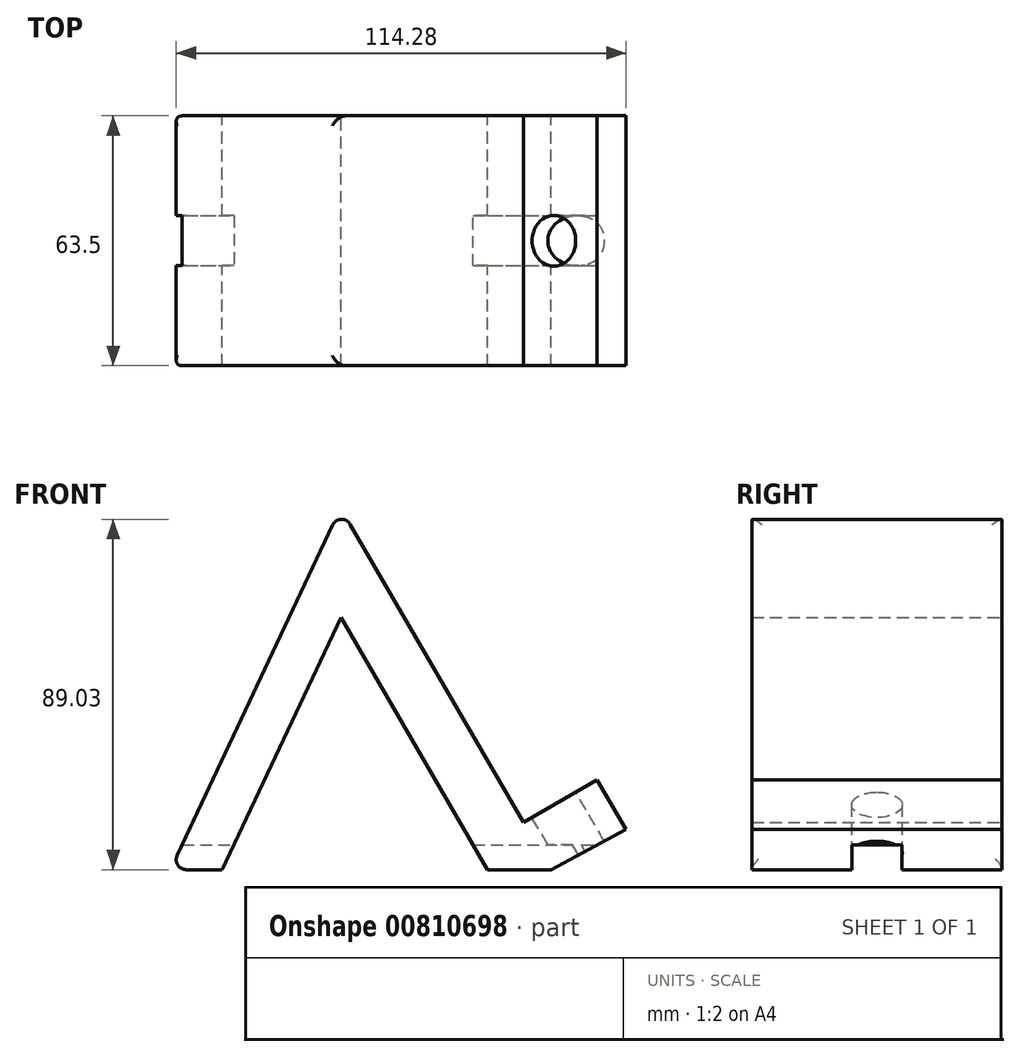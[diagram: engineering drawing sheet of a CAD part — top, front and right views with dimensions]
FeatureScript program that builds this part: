
annotation { "Feature Type Name" : "Feature", "Feature Type Description" : "" }
export const myFeature = defineFeature(function(context is Context, id is Id, definition is map)
    precondition{}
    {
        {
            var Q0;
            Q0=qCreatedBy(makeId("Front.planeOp"),FACE);
            var sketch = newSketch(context, id + "F0", { "sketchPlane" : qUnion([Q0])});
            skPoint(sketch, "E0.end.orphan", {"position": v(14.83, 0) * mm});
            skPoint(sketch, "E0.start.orphan", {"position": v(21.6, 0) * mm});
            skPoint(sketch, "E1.end.orphan", {"position": v(-8.7, 0) * mm});
            skPoint(sketch, "E2.end.orphan", {"position": v(-15.4, 9.9) * mm});
            skPoint(sketch, "E3.end.orphan", {"position": v(-27.26, 0) * mm});
            skPoint(sketch, "E4.end.orphan", {"position": v(-22.1, 19.8) * mm});
            skLineSegment(sketch, "E5", {"start": v(39.33, -93.18) * mm, "end": v(-7.17, -13.23) * mm});
            skLineSegment(sketch, "E6", {"start": v(-7.17, -13.23) * mm, "end": v(-50.38, -105.18) * mm});
            skPoint(sketch, "E7.end.orphan", {"position": v(-10.8, -21.16) * mm});
            skPoint(sketch, "E8.orphan", {"position": v(38.06, -105.18) * mm});
            skLineSegment(sketch, "E9", {"start": v(-10.8, -20.96) * mm, "end": v(-10.8, -21.16) * mm});
            skLineSegment(sketch, "E10", {"start": v(-50.38, -105.18) * mm, "end": v(-37.22, -105.18) * mm});
            skLineSegment(sketch, "E11", {"start": v(-37.22, -105.18) * mm, "end": v(-7.1, -41.1) * mm});
            skLineSegment(sketch, "E12", {"start": v(-7.1, -41.1) * mm, "end": v(30.16, -105.18) * mm});
            skLineSegment(sketch, "E13", {"start": v(30.16, -105.18) * mm, "end": v(46.3, -105.18) * mm});
            skPoint(sketch, "E14.end.orphan", {"position": v(-10.8, 22.67) * mm});
            skLineSegment(sketch, "E15", {"start": v(39.33, -93.18) * mm, "end": v(58, -82.32) * mm});
            skLineSegment(sketch, "E16", {"start": v(58, -82.32) * mm, "end": v(65.36, -94.95) * mm});
            skLineSegment(sketch, "E17", {"start": v(65.36, -94.95) * mm, "end": v(46.3, -105.18) * mm});
            skPoint(sketch, "E18.start.orphan", {"position": v(-71.03, -105.18) * mm});
            skLineSegment(sketch, "E19", {"start": v(-7.17, -13.23) * mm, "end": v(39.33, -93.18) * mm});
            skSolve(sketch);
        }
        {
            var Q0;
            Q0 = qSketchRegion(id + "F0", true);
            extrude(context, id + "F1", {"entities" : qUnion([Q0]), "depth" : 63.5 * mm, "offsetDistance" : 25.4 * mm});
        }
        {
            var Q0;
            Q0=makeQuery(id+"F1.opExtrude","SWEPT_FACE",FACE,{"disambiguationData":[OSD([sQuery(id+"F0.wireOp",EDGE,"E15")])]});
            var sketch = newSketch(context, id + "F2", { "sketchPlane" : qUnion([Q0])});
            skCircle(sketch, "E20", {"center": v(-3.96, -31.75) * mm, "radius": 6.42 * mm});
            skSolve(sketch);
        }
        {
            var Q0;
            Q0 = qSketchRegion(id + "F2", true);
            extrude(context, id + "F3", {"entities" : qUnion([Q0]), "operationType" : NewBodyOperationType.REMOVE, "endBound" : BoundingType.THROUGH_ALL, "oppositeDirection" : true, "depth" : 25.4 * mm, "offsetDistance" : 25.4 * mm});
        }
        {
            var Q0;
            Q0=makeQuery(id+"F1.opExtrude","SWEPT_FACE",FACE,{"disambiguationData":[OSD([sQuery(id+"F0.wireOp",EDGE,"E10")])]});
            var sketch = newSketch(context, id + "F4", { "sketchPlane" : qUnion([Q0])});
            skLineSegment(sketch, "E21.bottom", {"start": v(-51.41, 38.1) * mm, "end": v(73.47, 38.1) * mm});
            skLineSegment(sketch, "E21.top", {"start": v(-51.41, 25.4) * mm, "end": v(73.47, 25.4) * mm});
            skLineSegment(sketch, "E21.left", {"start": v(-51.41, 38.1) * mm, "end": v(-51.41, 25.4) * mm});
            skLineSegment(sketch, "E21.right", {"start": v(73.47, 38.1) * mm, "end": v(73.47, 25.4) * mm});
            skSolve(sketch);
        }
        {
            var Q0;
            Q0 = qSketchRegion(id + "F4", true);
            extrude(context, id + "F5", {"entities" : qUnion([Q0]), "operationType" : NewBodyOperationType.REMOVE, "oppositeDirection" : true, "depth" : 6.35 * mm, "offsetDistance" : 25.4 * mm});
        }
        {
            var Q0;
            Q0=makeQuery(id+"F1.opExtrude","SWEPT_EDGE",EDGE,{"disambiguationData":[OSD([sQuery(id+"F0.wireOp",EDGE,"E6"),sQuery(id+"F0.wireOp",EDGE,"E19")])]});
            var Q1;
            Q1=makeQuery(id+"F1.opExtrude","CAP_EDGE",EDGE,{"disambiguationData":[OSD([sQuery(id+"F0.wireOp",EDGE,"E19")])],"isStart":false});
            var Q2;
            Q2=makeQuery(id+"F1.opExtrude","CAP_EDGE",EDGE,{"disambiguationData":[OSD([sQuery(id+"F0.wireOp",EDGE,"E19")])],"isStart":true});
            var Q3;
            Q3=makeQuery(id+"F1.opExtrude","CAP_EDGE",EDGE,{"disambiguationData":[OSD([sQuery(id+"F0.wireOp",EDGE,"E6")])],"isStart":false});
            var Q4;
            Q4=makeQuery(id+"F1.opExtrude","CAP_EDGE",EDGE,{"disambiguationData":[OSD([sQuery(id+"F0.wireOp",EDGE,"E6")])],"isStart":true});
            fillet(context, id + "F6", {"entities" : qUnion([Q0, Q1, Q2, Q3, Q4]), "radius" : 2.54 * mm, "tangentPropagation" : true, "allowEdgeOverflow" : false});
        }
    });
